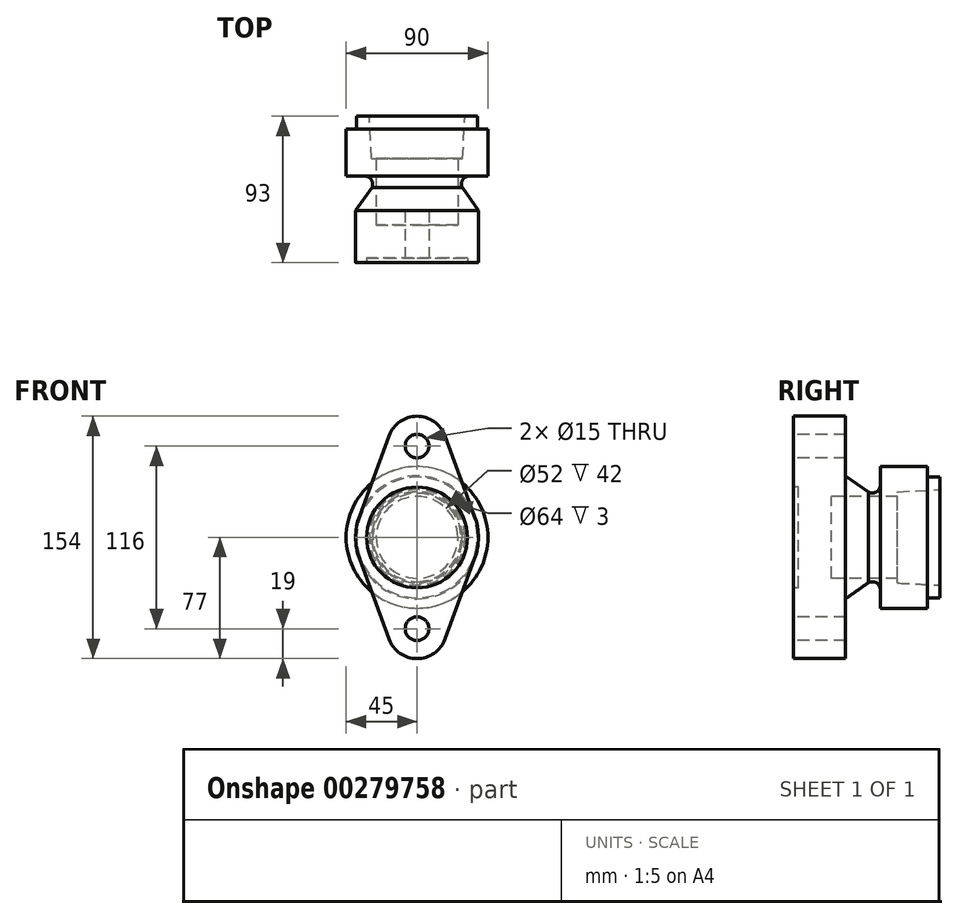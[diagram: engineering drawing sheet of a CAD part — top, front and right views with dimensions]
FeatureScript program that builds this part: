
annotation { "Feature Type Name" : "Feature", "Feature Type Description" : "" }
export const myFeature = defineFeature(function(context is Context, id is Id, definition is map)
    precondition{}
    {
        {
            var Q0;
            Q0=qCreatedBy(makeId("Right.planeOp"),FACE);
            var sketch = newSketch(context, id + "F0", { "sketchPlane" : qUnion([Q0])});
            skLineSegment(sketch, "E0", {"start": v(0, 0) * mm, "end": v(3, 0) * mm});
            skLineSegment(sketch, "E1", {"start": v(3, 0) * mm, "end": v(3, 32) * mm});
            skLineSegment(sketch, "E2", {"start": v(3, 32) * mm, "end": v(0, 32) * mm});
            skLineSegment(sketch, "E3", {"start": v(0, 32) * mm, "end": v(0, 39) * mm});
            skLineSegment(sketch, "E4", {"start": v(0, 39) * mm, "end": v(33, 39) * mm});
            skLineSegment(sketch, "E5", {"start": v(3, 0) * mm, "end": v(24, 0) * mm});
            skLineSegment(sketch, "E6", {"start": v(24, 0) * mm, "end": v(24, 26) * mm});
            skLineSegment(sketch, "E7", {"start": v(24, 26) * mm, "end": v(66, 26) * mm});
            skLineSegment(sketch, "E8", {"start": v(66, 26) * mm, "end": v(66, 29) * mm});
            skLineSegment(sketch, "E9", {"start": v(66, 29) * mm, "end": v(93, 30.34) * mm});
            skPoint(sketch, "E10.start.orphan", {"position": v(93, 0) * mm});
            skPoint(sketch, "E11.end.orphan", {"position": v(93, 36.84) * mm});
            skLineSegment(sketch, "E12", {"start": v(93, 30.34) * mm, "end": v(93, 38.34) * mm});
            skLineSegment(sketch, "E13", {"start": v(93, 38.34) * mm, "end": v(85, 38.34) * mm});
            skLineSegment(sketch, "E14", {"start": v(55, 45) * mm, "end": v(85, 45) * mm});
            skLineSegment(sketch, "E15", {"start": v(85, 45) * mm, "end": v(85, 38.34) * mm});
            skPoint(sketch, "E16.orphan", {"position": v(79.89, 38.34) * mm});
            skPoint(sketch, "E17.start.orphan", {"position": v(33, 57.47) * mm});
            skPoint(sketch, "E18.visualSharp", {"position": v(33, 26.28) * mm});
            skLineSegment(sketch, "E19", {"start": v(55, 38.34) * mm, "end": v(55, 45) * mm});
            skLineSegment(sketch, "E20", {"start": v(55, 38.34) * mm, "end": v(55, 33.16) * mm});
            skArc(sketch, "E21", {"start": v(47.64, 28.75) * mm, "mid": v(52.57, 28.87) * mm, "end": v(55, 33.16) * mm});
            skLineSegment(sketch, "E22", {"start": v(47.64, 28.75) * mm, "end": v(33, 39) * mm});
            skSolve(sketch);
        }
        {
            var Q0;
            Q0=makeQuery(id+"F0.imprint","IMPRINT",FACE,{"disambiguationData":[TD([[makeQuery(id+"F0.imprint","IMPRINT",EDGE,{"derivedFrom":sQuery(id+"F0.wireOp",EDGE,"E1")}),-1.0]])]});
            var Q1;
            Q1=sQuery(id+"F0.wireOp",EDGE,"E5");
            revolve(context, id + "F1", {"entities" : qUnion([Q0]), "axis" : qUnion([Q1]), "revolveType" : RevolveType.FULL});
        }
        {
            var Q0;
            Q0=makeQuery(id+"F1.opRevolve","SWEPT_FACE",FACE,{"disambiguationData":[OSD([sQuery(id+"F0.wireOp",EDGE,"E3")])]});
            var sketch = newSketch(context, id + "F2", { "sketchPlane" : qUnion([Q0])});
            skLineSegment(sketch, "E23", {"start": v(0, 0) * mm, "end": v(0, 77) * mm, "construction": true});
            skLineSegment(sketch, "E24", {"start": v(0, 50.5) * mm, "end": v(0, 0) * mm, "construction": true});
            skLineSegment(sketch, "E25", {"start": v(-13.43, 58) * mm, "end": v(16, 58) * mm, "construction": true});
            skCircle(sketch, "E26", {"center": v(0, 58) * mm, "radius": 7.5 * mm});
            skArc(sketch, "E27", {"start": v(17.83, 64.55) * mm, "mid": v(0, 77) * mm, "end": v(-17.83, 64.55) * mm});
            skPoint(sketch, "E28.end.orphan", {"position": v(-36.6, 13.45) * mm});
            skPoint(sketch, "E28.start.orphan", {"position": v(-19, 58) * mm});
            skPoint(sketch, "E29.end.orphan", {"position": v(36.6, 13.45) * mm});
            skPoint(sketch, "E29.start.orphan", {"position": v(19, 58) * mm});
            skLineSegment(sketch, "E30", {"start": v(-17.83, 64.55) * mm, "end": v(-36.6, 13.45) * mm});
            skLineSegment(sketch, "E31", {"start": v(36.6, 13.45) * mm, "end": v(17.83, 64.55) * mm});
            skCircle(sketch, "E32", {"center": v(0, 0) * mm, "radius": 39 * mm});
            skLineSegment(sketch, "E33", {"start": v(-73.73, 0) * mm, "end": v(75.5, 0) * mm, "construction": true});
            skLineSegment(sketch, "E34.MirrorCS", {"start": v(36.6, -13.45) * mm, "end": v(17.83, -64.55) * mm});
            skArc(sketch, "E35.MirrorCS", {"start": v(17.83, -64.55) * mm, "mid": v(0, -77) * mm, "end": v(-17.83, -64.55) * mm});
            skLineSegment(sketch, "E36.MirrorCS", {"start": v(-17.83, -64.55) * mm, "end": v(-36.6, -13.45) * mm});
            skArc(sketch, "E37.MirrorC", {"start": v(-36.6, 13.45) * mm, "mid": v(-22.32, 31.98) * mm, "end": v(0, 39) * mm});
            skCircle(sketch, "E38.MirrorC", {"center": v(0, -58) * mm, "radius": 7.5 * mm});
            skLineSegment(sketch, "E39.MirrorCS", {"start": v(-13.43, -58) * mm, "end": v(16, -58) * mm, "construction": true});
            skArc(sketch, "E40.trimOffspring", {"start": v(39, 0) * mm, "mid": v(6.83, -38.4) * mm, "end": v(-36.6, -13.45) * mm});
            skSolve(sketch);
        }
        {
            var Q0;
            Q0=makeQuery(id+"F2.imprint","IMPRINT",FACE,{"disambiguationData":[TD([[makeQuery(id+"F2.imprint","IMPRINT",EDGE,{"derivedFrom":sQuery(id+"F2.wireOp",EDGE,"E26")}),-1.0]])]});
            var Q1;
            {var subQ1=sQuery(id+"F2.wireOp",EDGE,"E34.MirrorCS");Q1=makeQuery(id+"F2.imprint","IMPRINT",FACE,{"disambiguationData":[TD([[makeQuery(id+"F2.imprint","IMPRINT",EDGE,{"derivedFrom":subQ1}),-1.0]])]});}
            extrude(context, id + "F3", {"entities" : qUnion([Q0, Q1]), "operationType" : NewBodyOperationType.ADD, "oppositeDirection" : true, "depth" : 33 * mm});
        }
    });
